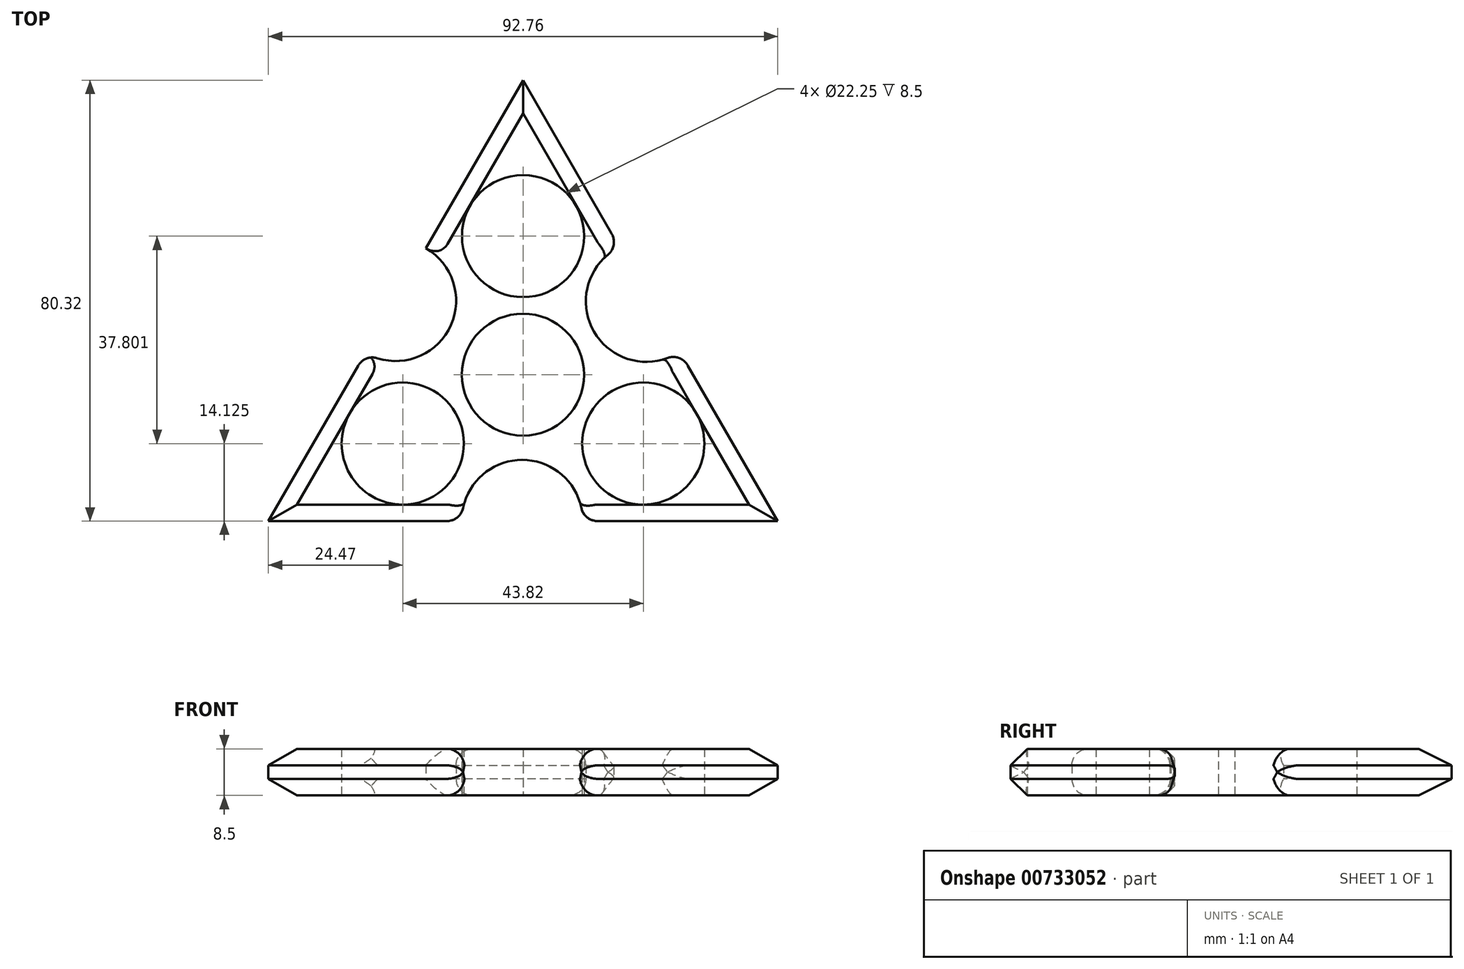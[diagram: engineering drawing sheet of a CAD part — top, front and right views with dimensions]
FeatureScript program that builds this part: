
annotation { "Feature Type Name" : "Feature", "Feature Type Description" : "" }
export const myFeature = defineFeature(function(context is Context, id is Id, definition is map)
    precondition{}
    {
        {
            var Q0;
            Q0=qCreatedBy(makeId("Top.planeOp"),FACE);
            var sketch = newSketch(context, id + "F0", { "sketchPlane" : qUnion([Q0])});
            skLineSegment(sketch, "E0", {"start": v(0, 80.32) * mm, "end": v(-17.69, 49.69) * mm});
            skLineSegment(sketch, "E1", {"start": v(-46.38, 0) * mm, "end": v(-11.14, 0) * mm});
            skLineSegment(sketch, "E2", {"start": v(0, 80.32) * mm, "end": v(17.57, 49.88) * mm});
            skPoint(sketch, "E3", {"position": v(0, 26.68) * mm});
            skCircle(sketch, "E4", {"center": v(0, 26.68) * mm, "radius": 11.12 * mm});
            skCircle(sketch, "E5", {"center": v(-21.9, 14.12) * mm, "radius": 11.12 * mm});
            skCircle(sketch, "E6", {"center": v(21.9, 14.13) * mm, "radius": 11.12 * mm});
            skCircle(sketch, "E7", {"center": v(0, 51.93) * mm, "radius": 11.12 * mm});
            skArc(sketch, "E8", {"start": v(-28.69, 30.64) * mm, "mid": v(-13.66, 34.66) * mm, "end": v(-17.69, 49.69) * mm});
            skArc(sketch, "E9", {"start": v(10.86, 0) * mm, "mid": v(-0.14, 11.15) * mm, "end": v(-11.14, 0) * mm});
            skPoint(sketch, "E10", {"position": v(23.19, 40.16) * mm});
            skArc(sketch, "E11", {"start": v(17.57, 49.88) * mm, "mid": v(12.92, 34.52) * mm, "end": v(28.55, 30.87) * mm});
            skPoint(sketch, "E12", {"position": v(-17.69, 49.69) * mm});
            skPoint(sketch, "E13", {"position": v(-28.69, 30.64) * mm});
            skLineSegment(sketch, "E14.trimOffspring", {"start": v(-28.69, 30.64) * mm, "end": v(-46.37, 0) * mm});
            skLineSegment(sketch, "E15.trimOffspring", {"start": v(28.55, 30.87) * mm, "end": v(46.38, 0) * mm});
            skPoint(sketch, "E16", {"position": v(28.55, 30.87) * mm});
            skPoint(sketch, "E17", {"position": v(10.86, 0) * mm});
            skPoint(sketch, "E18", {"position": v(-11.14, 0) * mm});
            skLineSegment(sketch, "E19.trimOffspring", {"start": v(10.86, 0) * mm, "end": v(46.38, 0) * mm});
            skSolve(sketch);
        }
        {
            var Q0;
            Q0 = qSketchRegion(id + "F0", true);
            extrude(context, id + "F1", {"entities" : qUnion([Q0]), "depth" : 8.5 * mm, "offsetDistance" : 25 * mm});
        }
        {
            var Q0;
            Q0=makeQuery(id+"F1.opExtrude","CAP_EDGE",EDGE,{"disambiguationData":[OSD([sQuery(id+"F0.wireOp",EDGE,"E0")])],"isStart":true});
            var Q1;
            Q1=makeQuery(id+"F1.opExtrude","CAP_EDGE",EDGE,{"disambiguationData":[OSD([sQuery(id+"F0.wireOp",EDGE,"E2")])],"isStart":false});
            var Q2;
            Q2=makeQuery(id+"F1.opExtrude","CAP_EDGE",EDGE,{"disambiguationData":[OSD([sQuery(id+"F0.wireOp",EDGE,"E2")])],"isStart":true});
            var Q3;
            Q3=makeQuery(id+"F1.opExtrude","CAP_EDGE",EDGE,{"disambiguationData":[OSD([sQuery(id+"F0.wireOp",EDGE,"E0")])],"isStart":false});
            var Q4;
            Q4=makeQuery(id+"F1.opExtrude","CAP_EDGE",EDGE,{"disambiguationData":[OSD([sQuery(id+"F0.wireOp",EDGE,"E15.trimOffspring")])],"isStart":false});
            var Q5;
            Q5=makeQuery(id+"F1.opExtrude","CAP_EDGE",EDGE,{"disambiguationData":[OSD([sQuery(id+"F0.wireOp",EDGE,"E15.trimOffspring")])],"isStart":true});
            var Q6;
            Q6=makeQuery(id+"F1.opExtrude","CAP_EDGE",EDGE,{"disambiguationData":[OSD([sQuery(id+"F0.wireOp",EDGE,"E19.trimOffspring")])],"isStart":false});
            var Q7;
            Q7=makeQuery(id+"F1.opExtrude","CAP_EDGE",EDGE,{"disambiguationData":[OSD([sQuery(id+"F0.wireOp",EDGE,"E19.trimOffspring")])],"isStart":true});
            var Q8;
            Q8=makeQuery(id+"F1.opExtrude","CAP_EDGE",EDGE,{"disambiguationData":[OSD([sQuery(id+"F0.wireOp",EDGE,"E1")])],"isStart":false});
            var Q9;
            Q9=makeQuery(id+"F1.opExtrude","CAP_EDGE",EDGE,{"disambiguationData":[OSD([sQuery(id+"F0.wireOp",EDGE,"E1")])],"isStart":true});
            var Q10;
            Q10=makeQuery(id+"F1.opExtrude","CAP_EDGE",EDGE,{"disambiguationData":[OSD([sQuery(id+"F0.wireOp",EDGE,"E14.trimOffspring")])],"isStart":true});
            var Q11;
            Q11=makeQuery(id+"F1.opExtrude","CAP_EDGE",EDGE,{"disambiguationData":[OSD([sQuery(id+"F0.wireOp",EDGE,"E14.trimOffspring")])],"isStart":false});
            chamfer(context, id + "F2", {"entities" : qUnion([Q0, Q1, Q2, Q3, Q4, Q5, Q6, Q7, Q8, Q9, Q10, Q11]), "width" : 3 * mm, "tangentPropagation" : true});
        }
        {
            var Q0;
            Q0=makeQuery(id+"F1.opExtrude","CAP_EDGE",EDGE,{"disambiguationData":[OSD([sQuery(id+"F0.wireOp",EDGE,"E8")])],"isStart":false});
            var Q1;
            Q1=makeQuery(id+"F1.opExtrude","SWEPT_FACE",FACE,{"disambiguationData":[OSD([sQuery(id+"F0.wireOp",EDGE,"E11")])]});
            var Q2;
            Q2=makeQuery(id+"F1.opExtrude","SWEPT_FACE",FACE,{"disambiguationData":[OSD([sQuery(id+"F0.wireOp",EDGE,"E9")])]});
            var Q3;
            Q3=makeQuery(id+"F1.opExtrude","CAP_EDGE",EDGE,{"disambiguationData":[OSD([sQuery(id+"F0.wireOp",EDGE,"E8")])],"isStart":true});
            var Q4;
            Q4=makeQuery(id+"F1.opExtrude","SWEPT_EDGE",EDGE,{"disambiguationData":[OSD([sQuery(id+"F0.wireOp",EDGE,"E8"),sQuery(id+"F0.wireOp",EDGE,"E14.trimOffspring")])]});
            fillet(context, id + "F3", {"entities" : qUnion([Q0, Q1, Q2, Q3, Q4]), "radius" : 3 * mm, "tangentPropagation" : true, "allowEdgeOverflow" : false});
        }
    });
